# Revit family: 0043210 Sylvania Lighting Fixture SYLMIRROR LED FLUTE IP44 NW Horizontal mount
name_source: partatom
category: Lighting Fixtures
revit_build: Autodesk Revit 2016 (Build: 20150220_1215(x64)
units: mm (PartAtom-declared; Revit-internal decimal feet)

## family parameters
Cut with Voids When Loaded = No
Host = Face
Light Source = No
OmniClass Number = 23.80.70.00
OmniClass Title = Lighting
Part Type = Normal
Room Calculation Point = No
Round Connector Dimension = Use Diameter
Shared = No

## types (1)
- 0043210 SYLMIRROR LED FLUTE IP44 NW Horizontal mount
    Apparent Load = 6 VA
    Assembly Code = D5020200
    AssetType = Fixed
    ClassificationName = Uniclass2015
    ClassificationValue = EF_70_80
    Cost = 0 $
    Default Elevation = 1219 mm
    DocumentationLiterature = http://www.sylvania-lighting.com
    DurationUnit = hours
    ElectricShockClassification = Class II
    ExpectedLife = 50000
    IfcExportAs = IfcLightFixtureType
    IfcExportType = IfcLightFixtureType
    ImpactProtectionIndex = IK03
    IngressProtection = IP44
    InputNominalFrequency = 50/60 Hz
    InputVoltage = 220-240V~
    Keynote = 16500
    Lamp = LED
    LampColourRenderingIndex = 80
    LampColourTemperature = 4000 K
    LampMacAdamStep = 6
    LampNominalLuminous = 540 lm
    LampsType = LED
    LightOutputRatio = 100
    LuminousEfficacy = 90 lm/W
    Manufacturer = Feilo Sylvania
    ManufacturerName = Feilo Sylvania
    Material = pc housing, pc diffuser
    Material_1_FEILO = Body-Sylvania-SylMirror
    Material_2_FEILO = Diffuser-Sylvania-SylMirror
    Material_3_FEILO = <By Category>
    Material_4_FEILO = <By Category>
    Model = SYLMIRROR LED FLUTE IP44 NW Horizontal mount
    ModelNumber = 0043210
    ModelReference = SYLMIRROR LED FLUTE IP44 NW Horizontal mount
    Name = SYLMIRROR LED FLUTE IP44 NW Horizontal mount
    NominalDepth = 115 mm
    NominalHeight = 53 mm
    NominalLength = 400 mm  [stored 1.31234 ft]
    PowerConsumption = 6 W
    PowerFactor = 0
    Type Image = <None>
    TypeLamp_SYL = SylMirror LED Flute : 0043210 SylMirror LED Flute
    TypeName = SYLMIRROR LED FLUTE IP44 NW Horizontal mount
    URL = http://www.sylvania-lighting.com
    Voltage = 230 V
    Weight = 0.606 kg

note: [stored X ft] marks values corroborated as IEEE doubles in the binary element streams (Revit-internal decimal feet)

## geometry (parser evidence)
native form markers: Sweep x5
no freeform markers — native parametric forms only
